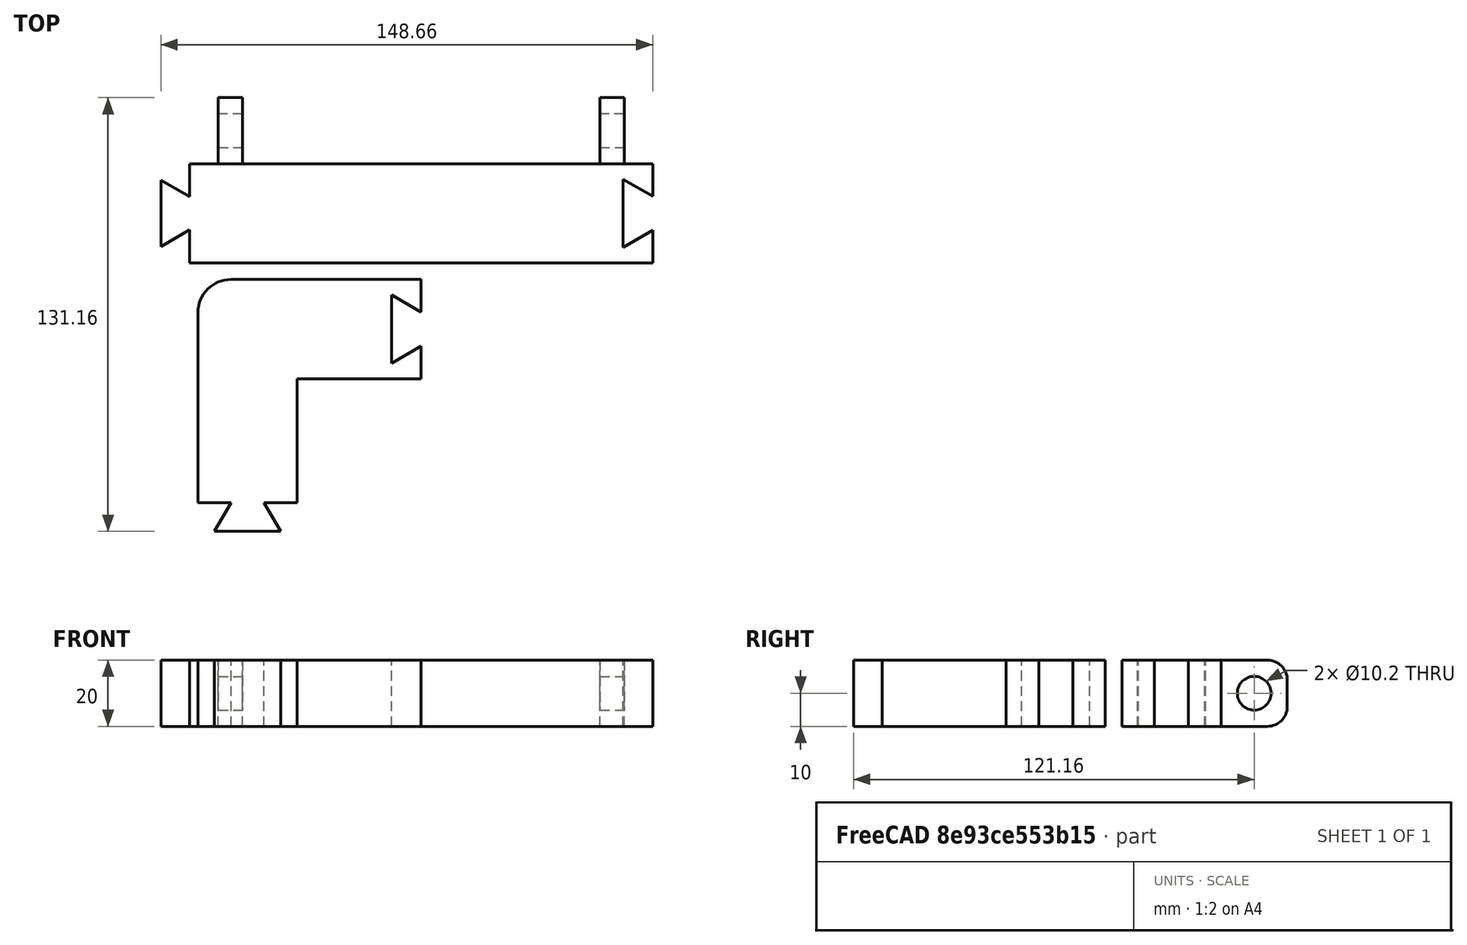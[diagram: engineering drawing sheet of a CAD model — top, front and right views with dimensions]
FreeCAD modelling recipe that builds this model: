
FCSTD DOCUMENT  (FreeCAD 0.21R33668 +26 (Git))
Label: board_holder
License: All rights reserved
LicenseURL: http://en.wikipedia.org/wiki/All_rights_reserved
objects: Sketcher::SketchObject×5, PartDesign::Pad×4, PartDesign::Body×4, App::Part×4, PartDesign::Fillet×3, Mesh::Feature×1, PartDesign::Pocket×1
note: 25 computed .brp shape members not serialized (recipe doc carries the construction recipe); baked Part::Feature solids carry a one-line shape summary decoded from their .brp

FEATURE [Mesh::Feature] gameboard_v0_1  label="gameboard_v0.1"
FEATURE [Sketcher::SketchObject] Sketch
  FullyConstrained = true
  MapMode = 5
  Support = -> [XY_Plane003]
  sketch-geometry (12):
    g0: LineSegment StartX=-70 StartY=15 StartZ=0 EndX=70 EndY=15 EndZ=0
    g1: LineSegment StartX=70 StartY=15 StartZ=0 EndX=70 EndY=5.15 EndZ=0
    g2: LineSegment StartX=70 StartY=-15 StartZ=0 EndX=-70 EndY=-15 EndZ=0
    g3: LineSegment StartX=-70 StartY=-15 StartZ=0 EndX=-70 EndY=-5 EndZ=0
    g4: LineSegment StartX=-70 StartY=5 StartZ=0 EndX=-78.6603 EndY=10 EndZ=0
    g5: LineSegment StartX=-70 StartY=-5 StartZ=0 EndX=-78.6603 EndY=-10 EndZ=0
    g6: LineSegment StartX=-78.6603 StartY=-10 StartZ=0 EndX=-78.6603 EndY=10 EndZ=0
    g7: LineSegment StartX=-70 StartY=5 StartZ=0 EndX=-70 EndY=15 EndZ=0
    g8: LineSegment StartX=70 StartY=5.15 StartZ=0 EndX=61.0799 EndY=10.3 EndZ=0
    g9: LineSegment StartX=70 StartY=-5.15 StartZ=0 EndX=61.0799 EndY=-10.3 EndZ=0
    g10: LineSegment StartX=61.0799 StartY=-10.3 StartZ=0 EndX=61.0799 EndY=10.3 EndZ=0
    g11: LineSegment StartX=70 StartY=-5.15 StartZ=0 EndX=70 EndY=-15 EndZ=0
  constraints (35):
    c: Coincident(g0,g1)
    c: Coincident(g11,g2)
    c: Coincident(g2,g3)
    c: Coincident(g7,g0)
    c: Horizontal(g0)
    c: Horizontal(g2)
    c: Vertical(g1)
    c: Vertical(g3)
    c: Symmetric(g0,g11,g-1)
    c: DistanceX(g0,g0) = 140
    c: Coincident(g6,g5)
    c: Coincident(g6,g4)
    c: Vertical(g6)
    c: Angle(g4,g3) = 2.0944
    c: Angle(g3,g5) = 2.0944
    c: Coincident(g3,g5)
    c: Coincident(g7,g4)
    c: Equal(g7,g3)
    c: Parallel(g7,g3)
    c: Equal(g0,g2)
    c: Distance(g7) = 10
    c: Distance(g6) = 20
    c: DistanceY(g2,g0) = 30
    c: Coincident(g10,g9)
    c: Coincident(g10,g8)
    c: Vertical(g10)
    c: Angle(g8,g1) = 2.0944
    c: Angle(g1,g9) = 2.0944
    c: Distance(g10) = 20.6
    c: Coincident(g1,g8)
    c: Coincident(g11,g9)
    c: Parallel(g1,g11)
    c: Equal(g1,g11)
    c: Distance(g1) = 9.85
    c: Equal(g8,g9)
FEATURE [PartDesign::Pad] Pad
  Direction = (0,0,1)
  Length = 20
  Length2 = 10
  Profile = -> Sketch
  ReferenceAxis = -> Sketch [N_Axis]
  Refine = true
  Type = 0
FEATURE [PartDesign::Body] Body
  Group = -> [Sketch,Pad]
  Origin = -> Origin003
  Tip = -> Pad
FEATURE [App::Part] Part001  label="blank side"
  Group = -> [Body]
  Origin = -> Origin001
  Placement = pos=(-15,106.5,0) rot=(0,0,1;1.5708rad)
FEATURE [Sketcher::SketchObject] Sketch001
  FullyConstrained = true
  MapMode = 5
  Support = -> [XY_Plane004]
  sketch-geometry (20):
    g0: LineSegment StartX=-70 StartY=15 StartZ=0 EndX=-61.4 EndY=15 EndZ=0
    g1: LineSegment StartX=70 StartY=15 StartZ=0 EndX=70 EndY=5.15 EndZ=0
    g2: LineSegment StartX=70 StartY=-15 StartZ=0 EndX=-70 EndY=-15 EndZ=0
    g3: LineSegment StartX=-70 StartY=-15 StartZ=0 EndX=-70 EndY=-5 EndZ=0
    g4: LineSegment StartX=-70 StartY=5 StartZ=0 EndX=-78.6603 EndY=10 EndZ=0
    g5: LineSegment StartX=-70 StartY=-5 StartZ=0 EndX=-78.6603 EndY=-10 EndZ=0
    g6: LineSegment StartX=-78.6603 StartY=-10 StartZ=0 EndX=-78.6603 EndY=10 EndZ=0
    g7: LineSegment StartX=-70 StartY=5 StartZ=0 EndX=-70 EndY=15 EndZ=0
    g8: LineSegment StartX=70 StartY=5.15 StartZ=0 EndX=61.0799 EndY=10.3 EndZ=0
    g9: LineSegment StartX=70 StartY=-5.15 StartZ=0 EndX=61.0799 EndY=-10.3 EndZ=0
    g10: LineSegment StartX=61.0799 StartY=-10.3 StartZ=0 EndX=61.0799 EndY=10.3 EndZ=0
    g11: LineSegment StartX=70 StartY=-5.15 StartZ=0 EndX=70 EndY=-15 EndZ=0
    g12: LineSegment StartX=-54 StartY=15 StartZ=0 EndX=-54 EndY=35 EndZ=0
    g13: LineSegment StartX=-61.4 StartY=15 StartZ=0 EndX=-61.4 EndY=35 EndZ=0
    g14: LineSegment StartX=-61.4 StartY=35 StartZ=0 EndX=-54 EndY=35 EndZ=0
    g15: LineSegment StartX=61.4 StartY=15 StartZ=0 EndX=61.4 EndY=35 EndZ=0
    g16: LineSegment StartX=54 StartY=15 StartZ=0 EndX=54 EndY=35 EndZ=0
    g17: LineSegment StartX=54 StartY=35 StartZ=0 EndX=61.4 EndY=35 EndZ=0
    g18: LineSegment StartX=61.4 StartY=15 StartZ=0 EndX=70 EndY=15 EndZ=0
    g19: LineSegment StartX=-54 StartY=15 StartZ=0 EndX=54 EndY=15 EndZ=0
  constraints (59):
    c: Coincident(g18,g1)
    c: Coincident(g11,g2)
    c: Coincident(g2,g3)
    c: Coincident(g7,g0)
    c: Horizontal(g0)
    c: Horizontal(g2)
    c: Vertical(g1)
    c: Vertical(g3)
    c: Symmetric(g0,g11,g-1)
    c: DistanceX(g2,g2) = 140
    c: DistanceY(g2,g0) = 30
    c: Coincident(g6,g5)
    c: Coincident(g6,g4)
    c: Vertical(g6)
    c: Equal(g4,g5)
    c: Angle(g4,g3) = 2.0944
    c: Distance(g6) = 20
    c: Coincident(g3,g5)
    c: Coincident(g7,g4)
    c: Equal(g7,g3)
    c: Parallel(g7,g3)
    c: Distance(g7) = 10
    c: Angle(g5,g3) = 1.0472
    c: Coincident(g10,g9)
    c: Coincident(g10,g8)
    c: Vertical(g10)
    c: DistanceY(g10,g10) = 20.6
    c: Coincident(g1,g8)
    c: Coincident(g11,g9)
    c: Parallel(g11,g1)
    c: Equal(g1,g11)
    c: DistanceY(g1,g1) = 9.85
    c: Angle(g1,g8) = 1.0472
    c: Angle(g9,g11) = 1.0472
    c: Vertical(g12)
    c: Vertical(g13)
    c: Coincident(g14,g13)
    c: Coincident(g14,g12)
    c: Vertical(g15)
    c: Vertical(g16)
    c: Coincident(g17,g16)
    c: Coincident(g17,g15)
    c: Horizontal(g14)
    c: Horizontal(g17)
    c: Equal(g14,g17)
    c: Distance(g14) = 7.4
    c: Distance(g12,g-2) = 54
    c: Equal(g12,g16)
    c: Distance(g12,g16) = 108
    c: Distance(g12) = 20
    c: Coincident(g19,g16)
    c: Coincident(g18,g15)
    c: Coincident(g0,g13)
    c: Coincident(g19,g12)
    c: DistanceY(g0,g12) = 0
    c: DistanceY(g15,g16) = 0
    c: Horizontal(g19)
    c: Parallel(g19,g18)
    c: Equal(g0,g18)
FEATURE [PartDesign::Pad] Pad001
  Direction = (0,0,1)
  Length = 20
  Length2 = 10
  Profile = -> Sketch001
  ReferenceAxis = -> Sketch001 [N_Axis]
  Refine = true
  Type = 0
FEATURE [Sketcher::SketchObject] Sketch002
  ExternalGeometry = -> [Pad001]
  FullyConstrained = true
  MapMode = 5
  Placement = pos=(61.4,0,0) rot=(0.57735,0.57735,0.57735;2.0944rad)
  Support = -> [Pad001]
  sketch-geometry (5):
    g0: Circle CenterX=25 CenterY=10 CenterZ=0 NormalX=0 NormalY=0 NormalZ=1 AngleXU=0 Radius=5.1
    g1: LineSegment StartX=25 StartY=10 StartZ=0 EndX=25 EndY=20 EndZ=0
    g2: LineSegment StartX=25 StartY=10 StartZ=0 EndX=35 EndY=10 EndZ=0
    g3: LineSegment StartX=25 StartY=10 StartZ=0 EndX=15 EndY=10 EndZ=0
    g4: LineSegment StartX=25 StartY=10 StartZ=0 EndX=25 EndY=0 EndZ=0
  constraints (15):
    c: Diameter(g0) = 10.2
    c: Coincident(g1,g0)
    c: PointOnObject(g1,g-3)
    c: Coincident(g2,g0)
    c: PointOnObject(g2,g-5)
    c: Horizontal(g2)
    c: Coincident(g3,g0)
    c: PointOnObject(g3,g-6)
    c: Coincident(g4,g0)
    c: PointOnObject(g4,g-4)
    c: Parallel(g1,g4)
    c: Parallel(g3,g2)
    c: Vertical(g1)
    c: Equal(g1,g4)
    c: Equal(g2,g3)
FEATURE [PartDesign::Pocket] Pocket
  BaseFeature = -> Pad001
  Direction = (-1,0,0)
  Length = 200
  Length2 = 5
  Profile = -> Sketch002
  ReferenceAxis = -> Sketch002 [N_Axis]
  Refine = true
  Type = 0
FEATURE [PartDesign::Fillet] Fillet
  Base = -> Pocket [Edge33,Edge16,Edge12,Edge29]
  BaseFeature = -> Pocket
  Radius = 6
  Refine = true
  SupportTransform = false
  UseAllEdges = false
FEATURE [PartDesign::Body] Body001
  Group = -> [Sketch001,Pad001,Sketch002,Pocket,Fillet]
  Origin = -> Origin004
  Tip = -> Fillet
FEATURE [App::Part] Part002  label="mount side"
  Group = -> [Body001]
  Origin = -> Origin002
  Placement = pos=(107.5,229,0) rot=(0,0,1;0rad)
FEATURE [Sketcher::SketchObject] Sketch003
  FullyConstrained = true
  MapMode = 5
  Support = -> [XY_Plane005]
  sketch-geometry (14):
    g0: LineSegment StartX=0 StartY=30 StartZ=0 EndX=-67.5 EndY=30 EndZ=0
    g1: LineSegment StartX=-67.5 StartY=30 StartZ=0 EndX=-67.5 EndY=-37.5 EndZ=0
    g2: LineSegment StartX=-67.5 StartY=-37.5 StartZ=0 EndX=-57.5 EndY=-37.5 EndZ=0
    g3: LineSegment StartX=-37.5 StartY=-37.5 StartZ=0 EndX=-37.5 EndY=0 EndZ=0
    g4: LineSegment StartX=-37.5 StartY=0 StartZ=0 EndX=0 EndY=0 EndZ=0
    g5: LineSegment StartX=0 StartY=0 StartZ=0 EndX=0 EndY=9.85 EndZ=0
    g6: LineSegment StartX=-57.5 StartY=-37.5 StartZ=0 EndX=-62.5 EndY=-46.1603 EndZ=0
    g7: LineSegment StartX=-47.5 StartY=-37.5 StartZ=0 EndX=-42.5 EndY=-46.1603 EndZ=0
    g8: LineSegment StartX=-42.5 StartY=-46.1603 StartZ=0 EndX=-62.5 EndY=-46.1603 EndZ=0
    g9: LineSegment StartX=0 StartY=20.15 StartZ=0 EndX=-8.92006 EndY=25.3 EndZ=0
    g10: LineSegment StartX=0 StartY=9.85 StartZ=0 EndX=-8.92006 EndY=4.7 EndZ=0
    g11: LineSegment StartX=-8.92006 StartY=4.7 StartZ=0 EndX=-8.92006 EndY=25.3 EndZ=0
    g12: LineSegment StartX=0 StartY=20.15 StartZ=0 EndX=0 EndY=30 EndZ=0
    g13: LineSegment StartX=-47.5 StartY=-37.5 StartZ=0 EndX=-37.5 EndY=-37.5 EndZ=0
  constraints (41):
    c: Coincident(g1,g0)
    c: Coincident(g2,g1)
    c: Coincident(g3,g13)
    c: Horizontal(g4)
    c: Coincident(g5,g4)
    c: Coincident(g12,g0)
    c: Horizontal(g2)
    c: Horizontal(g0)
    c: Equal(g4,g3)
    c: Coincident(g3,g4)
    c: Vertical(g3)
    c: Vertical(g1)
    c: Vertical(g5)
    c: Equal(g0,g1)
    c: Coincident(g4,g-1)
    c: Distance(g4) = 37.5
    c: Distance(g0,g4) = 30
    c: Coincident(g8,g7)
    c: Coincident(g8,g6)
    c: Horizontal(g8)
    c: Coincident(g11,g10)
    c: Coincident(g11,g9)
    c: Vertical(g11)
    c: Coincident(g5,g10)
    c: Coincident(g12,g9)
    c: Coincident(g2,g6)
    c: Coincident(g13,g7)
    c: Equal(g2,g13)
    c: Parallel(g2,g13)
    c: Parallel(g5,g12)
    c: Equal(g12,g5)
    c: Distance(g8) = 20
    c: Distance(g11) = 20.6
    c: Distance(g12) = 9.85
    c: Distance(g2) = 10
    c: DistanceY(g2,g7) = 0
    c: DistanceX(g9,g5) = 0
    c: Angle(g2,g6) = 1.0472
    c: Angle(g7,g13) = 1.0472
    c: Angle(g12,g9) = 1.0472
    c: Angle(g10,g5) = 1.0472
FEATURE [PartDesign::Pad] Pad002
  Direction = (0,0,1)
  Length = 20
  Length2 = 10
  Profile = -> Sketch003
  ReferenceAxis = -> Sketch003 [N_Axis]
  Refine = true
  Type = 0
FEATURE [PartDesign::Fillet] Fillet001
  Base = -> Pad002 [Edge5]
  BaseFeature = -> Pad002
  Radius = 10
  Refine = true
  SupportTransform = false
  UseAllEdges = false
FEATURE [PartDesign::Body] Body002
  Group = -> [Sketch003,Pad002,Fillet001]
  Origin = -> Origin005
  Placement = pos=(0,-50,0) rot=(0,1,0;0rad)
  Tip = -> Fillet001
FEATURE [App::Part] Part  label="corner"
  Group = -> [Body002]
  Origin = -> Origin
  Placement = pos=(-50,36.5,0) rot=(0,0,1;1.5708rad)
FEATURE [Sketcher::SketchObject] Sketch004
  FullyConstrained = true
  MapMode = 5
  Support = -> [XY_Plane007]
  sketch-geometry (14):
    g0: LineSegment StartX=0 StartY=30 StartZ=0 EndX=-67.5 EndY=30 EndZ=0
    g1: LineSegment StartX=-67.5 StartY=30 StartZ=0 EndX=-67.5 EndY=-37.5 EndZ=0
    g2: LineSegment StartX=-67.5 StartY=-37.5 StartZ=0 EndX=-57.5 EndY=-37.5 EndZ=0
    g3: LineSegment StartX=-37.5 StartY=-37.5 StartZ=0 EndX=-37.5 EndY=0 EndZ=0
    g4: LineSegment StartX=-37.5 StartY=0 StartZ=0 EndX=0 EndY=0 EndZ=0
    g5: LineSegment StartX=0 StartY=0 StartZ=0 EndX=0 EndY=9.85 EndZ=0
    g6: LineSegment StartX=-57.5 StartY=-37.5 StartZ=0 EndX=-62.5 EndY=-46.1603 EndZ=0
    g7: LineSegment StartX=-47.5 StartY=-37.5 StartZ=0 EndX=-42.5 EndY=-46.1603 EndZ=0
    g8: LineSegment StartX=-42.5 StartY=-46.1603 StartZ=0 EndX=-62.5 EndY=-46.1603 EndZ=0
    g9: LineSegment StartX=0 StartY=20.15 StartZ=0 EndX=-8.92006 EndY=25.3 EndZ=0
    g10: LineSegment StartX=0 StartY=9.85 StartZ=0 EndX=-8.92006 EndY=4.7 EndZ=0
    g11: LineSegment StartX=-8.92006 StartY=4.7 StartZ=0 EndX=-8.92006 EndY=25.3 EndZ=0
    g12: LineSegment StartX=0 StartY=20.15 StartZ=0 EndX=0 EndY=30 EndZ=0
    g13: LineSegment StartX=-47.5 StartY=-37.5 StartZ=0 EndX=-37.5 EndY=-37.5 EndZ=0
  constraints (41):
    c: Coincident(g1,g0)
    c: Coincident(g2,g1)
    c: Coincident(g3,g13)
    c: Horizontal(g4)
    c: Coincident(g5,g4)
    c: Coincident(g12,g0)
    c: Horizontal(g2)
    c: Horizontal(g0)
    c: Equal(g4,g3)
    c: Coincident(g3,g4)
    c: Vertical(g3)
    c: Vertical(g1)
    c: Vertical(g5)
    c: Equal(g0,g1)
    c: Coincident(g4,g-1)
    c: Distance(g4) = 37.5
    c: Distance(g0,g4) = 30
    c: Coincident(g8,g7)
    c: Coincident(g8,g6)
    c: Horizontal(g8)
    c: Coincident(g11,g10)
    c: Coincident(g11,g9)
    c: Vertical(g11)
    c: Coincident(g5,g10)
    c: Coincident(g12,g9)
    c: Coincident(g2,g6)
    c: Coincident(g13,g7)
    c: Equal(g2,g13)
    c: Parallel(g2,g13)
    c: Parallel(g5,g12)
    c: Equal(g12,g5)
    c: Distance(g8) = 20
    c: Distance(g11) = 20.6
    c: Distance(g12) = 9.85
    c: Distance(g2) = 10
    c: DistanceY(g2,g7) = 0
    c: DistanceX(g9,g5) = 0
    c: Angle(g2,g6) = 1.0472
    c: Angle(g7,g13) = 1.0472
    c: Angle(g12,g9) = 1.0472
    c: Angle(g10,g5) = 1.0472
FEATURE [PartDesign::Pad] Pad003
  Direction = (0,0,1)
  Length = 20
  Length2 = 10
  Profile = -> Sketch004
  ReferenceAxis = -> Sketch004 [N_Axis]
  Refine = true
  Type = 0
FEATURE [PartDesign::Fillet] Fillet002
  Base = -> Pad003 [Edge5]
  BaseFeature = -> Pad003
  Radius = 10
  Refine = true
  SupportTransform = false
  UseAllEdges = false
FEATURE [PartDesign::Body] Body003
  Group = -> [Sketch004,Pad003,Fillet002]
  Origin = -> Origin007
  Placement = pos=(0,-50,0) rot=(0,1,0;0rad)
  Tip = -> Fillet002
FEATURE [App::Part] Part003  label="corner001"
  Group = -> [Body003]
  Origin = -> Origin006
  Placement = pos=(37.5,264,0) rot=(0,0,1;0rad)
